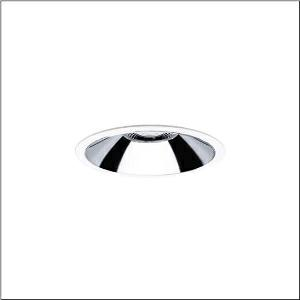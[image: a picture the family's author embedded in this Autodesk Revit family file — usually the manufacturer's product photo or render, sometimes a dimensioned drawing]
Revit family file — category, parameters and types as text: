
# Revit family: lunis_21_xl_51db15df33
name_source: partatom
category: Lighting Fixtures
units: mm (PartAtom-declared; Revit-internal decimal feet)

## family parameters
Cut with Voids When Loaded = No
Host = Face
Light Source = No
Part Type = Normal
Room Calculation Point = No
Round Connector Dimension = Use Diameter
Shared = No

## types (1)
- Lunis 21 XL (1 x LED, 3360 lm, 31 W, 3000K)
    Apparent Load = 31 VA
    CIE Flux Codes = 89 99 100 100 100
    Color Rendering = 80
    Color Temperature = 3000K
    Default Elevation = 1800 mm
    Description = Lunis 21,  XL, downlight, of PC, light emission: direct distribution, LED rated luminous flux: 3.360lm, light colour: 830, control gear: ECG DALI, with terminal, 5-pole, mains connection: 220..240V, AC, housing, round, of diecast aluminium, traffic white (RAL 9016), diameter: 213mm, protection rating (complete): IP20, protection rating (on room side): IP54, insulation class (complete): insulation class II (safety insulation), certification: CE, impact resistance: IK02, packaging unit: 1 piece
    Height = 0 mm  [stored 0 ft]
    Lamp = 1 x LED
    Lamp Light Flux = 3360 lm
    Lamp Power = 31 W
    Lamp count = 1
    Length = 213 mm
    Luminous efficacy = 108 lm/W
    Manufacturer = Siteco
    ModVariant = No
    Model = 51DB15DF33
    Mounting Place = Ceiling
    Mounting Type = Recessed
    Number of Poles = 1
    OnlyDefault = Yes
    Power Factor = 1
    Product Name = Lunis 21 XL
    Product group = downlight
    ProductGroupID = 400
    Protection Class = Protection class II
    Protection Degree = IP 20
    RLX_Detail_Level = 1
    RLX_Emergency_Light_Flux = 0 lm
    RLX_Emergency_Type = 0
    RLX_Emergency_Type_DB = No
    RlxData = <blob elided: 26989 chars, md5=85ff2222>
    Socket = socket
    Standby Power = 0 W
    System Light Flux = 3360 lm
    System Power = 31 W
    Type Comments = Product without accessories
    Type Image = l_1287385.jpg
    URL = http://relux.com
    VarID = ---
    Voltage = 0 V
    Weight = 0.00 kg
    Width = 0 mm  [stored 0 ft]

note: [stored X ft] marks values corroborated as IEEE doubles in the binary element streams (Revit-internal decimal feet)

## geometry (parser evidence)
native form markers: Blend x4, Sweep x11
no freeform markers — native parametric forms only
